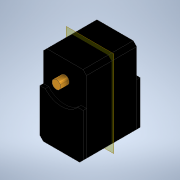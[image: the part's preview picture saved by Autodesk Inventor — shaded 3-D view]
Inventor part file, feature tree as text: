
AUTODESK INVENTOR PART (.ipt)
format: ipt  version: 2020.1 (Build 241239000, 239)  size: 168,448 bytes
history: native  units: mm
features: extrude x4, sketch x4, plane x2, chamfer x1, mirror x1
ambient origin geometry x8: Origin, YZ Plane, XZ Plane, XY Plane, X Axis, Y Axis, Z Axis, Center Point
bodies: Solid1 (feature_tree)
feature tree (12):
  extrude  "Extrusion1"  Depth=45.5mm
  chamfer  "Chamfer1"  Distance=29.0mm
  extrude  "Extrusion2"  Depth=12.5mm
  plane  "Work Plane1"
  extrude  "Extrusion3"  Depth=25.0mm
  mirror  "Mirror1"
  extrude  "Extrusion4"  Depth=5.0mm
  sketch  "Sketch1"  dims[d0=25.0mm d1=45.5mm d2=29.0mm d3=0.0mm]
  sketch  "Sketch2"  dims[d4=2.0mm d5=2.0mm d6=45.0deg d8=12.5mm]
  sketch  "Sketch3"  dims[d9=25.0mm d10=25.0mm]
  plane  "Work Plane2"
  sketch  "Sketch5"  dims[d11=2.0mm d12=0.0mm d13=5.0mm d14=5.0mm d15=0.0mm d16=13.0mm d17=10.0mm d18=5.0mm d19=20.0mm d20=5.0mm d21=0.0mm]
